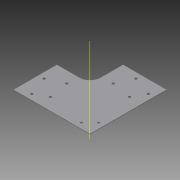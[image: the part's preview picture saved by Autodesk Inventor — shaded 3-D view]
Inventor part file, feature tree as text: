
AUTODESK INVENTOR PART (.ipt)
format: ipt  version: 2015 (Build 190159000, 159)  size: 105,472 bytes
history: native  units: in
note: dims shown in document units (in); Inventor stores cm internally (conversion verified against a paired STEP export)
features: extrude x1, plane x1, sketch x1
ambient origin geometry x8: Origin, YZ Plane, XZ Plane, XY Plane, X Axis, Y Axis, Z Axis, Center Point
bodies: Solid1 (feature_tree)
feature tree (3):
  extrude  "Extrusion1"  Depth=3.052in
  plane  "Work Plane1"
  sketch  "Sketch1"  dims[d0=5.384in d1=3.052in d2=0.75in d3=0.375in d6=0.375in d7=0.9in d8=0.4in d9=1.75in d10=0.175in d11=0.975in d12=1.5in d13=2.25in d14=0.85in d15=1.75in d16=0.035in d17=0.0in d18=90.0deg]
